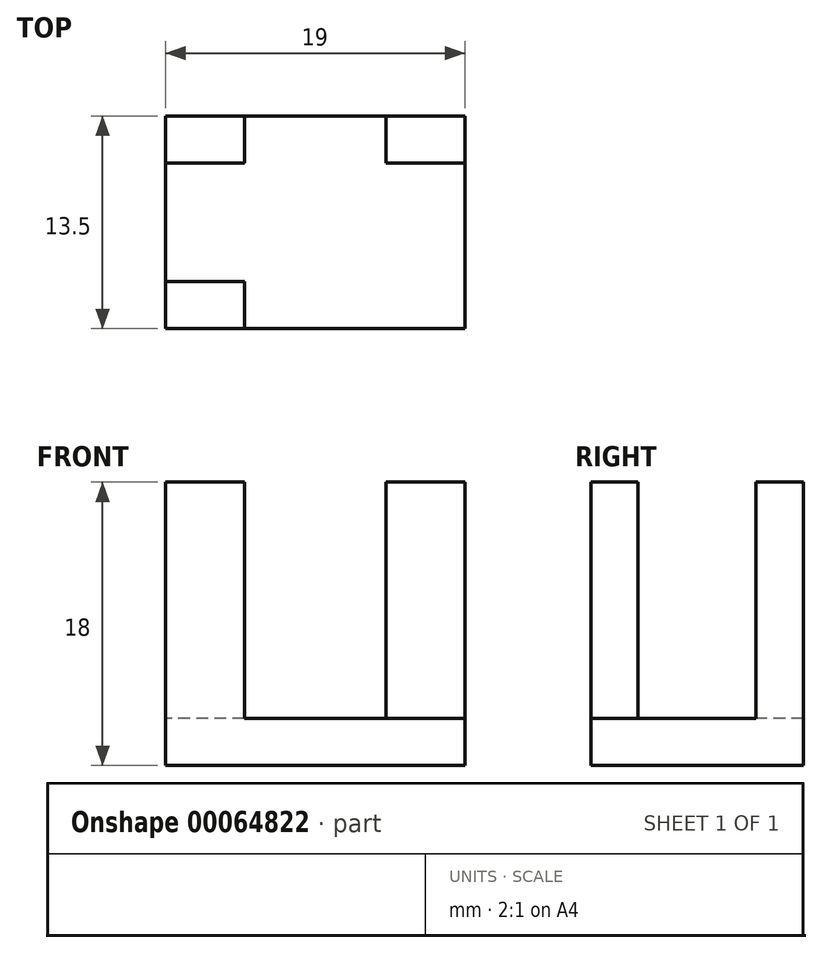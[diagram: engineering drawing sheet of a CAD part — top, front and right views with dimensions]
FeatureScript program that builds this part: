
annotation { "Feature Type Name" : "Feature", "Feature Type Description" : "" }
export const myFeature = defineFeature(function(context is Context, id is Id, definition is map)
    precondition{}
    {
        {
            var Q0;
            Q0=qCreatedBy(makeId("Top.planeOp"),FACE);
            var sketch = newSketch(context, id + "F0", { "sketchPlane" : qUnion([Q0])});
            skLineSegment(sketch, "E0.rect.bottom", {"start": v(-9.5, 6.75) * mm, "end": v(9.5, 6.75) * mm});
            skLineSegment(sketch, "E0.rect.top", {"start": v(-9.5, -6.75) * mm, "end": v(9.5, -6.75) * mm});
            skLineSegment(sketch, "E0.rect.left", {"start": v(-9.5, 6.75) * mm, "end": v(-9.5, -6.75) * mm});
            skLineSegment(sketch, "E0.rect.right", {"start": v(9.5, 6.75) * mm, "end": v(9.5, -6.75) * mm});
            skPoint(sketch, "E0.rect.middle", {"position": v(0, 0) * mm});
            skSolve(sketch);
        }
        {
            var Q0;
            Q0=makeQuery(id+"F0.imprint","IMPRINT",FACE,{"disambiguationData":[TD([[makeQuery(id+"F0.imprint","IMPRINT",EDGE,{"derivedFrom":sQuery(id+"F0.wireOp",EDGE,"E0.rect.bottom")}),-1.0]])]});
            extrude(context, id + "F1", {"entities" : qUnion([Q0]), "depth" : 3 * mm});
        }
        {
            var Q0;
            Q0=makeQuery(id+"F1.opExtrude","CAP_FACE",FACE,{"disambiguationData":[OSD([sQuery(id+"F0.wireOp",EDGE,"E0.rect.bottom"),sQuery(id+"F0.wireOp",EDGE,"E0.rect.top"),sQuery(id+"F0.wireOp",EDGE,"E0.rect.left"),sQuery(id+"F0.wireOp",EDGE,"E0.rect.right")])],"isStart":false});
            var sketch = newSketch(context, id + "F2", { "sketchPlane" : qUnion([Q0])});
            skLineSegment(sketch, "E1.bottom", {"start": v(9.5, 6.75) * mm, "end": v(4.5, 6.75) * mm});
            skLineSegment(sketch, "E1.top", {"start": v(9.5, -6.75) * mm, "end": v(4.5, -6.75) * mm});
            skLineSegment(sketch, "E1.left", {"start": v(9.5, 6.75) * mm, "end": v(9.5, -6.75) * mm});
            skLineSegment(sketch, "E1.right", {"start": v(4.5, 6.75) * mm, "end": v(4.5, -6.75) * mm});
            skLineSegment(sketch, "E2.top", {"start": v(9.5, 3.75) * mm, "end": v(4.5, 3.75) * mm});
            skLineSegment(sketch, "E2.left", {"start": v(9.5, 6.75) * mm, "end": v(9.5, 3.75) * mm});
            skLineSegment(sketch, "E2.right", {"start": v(4.5, 6.75) * mm, "end": v(4.5, 3.75) * mm});
            skLineSegment(sketch, "E3.bottom", {"start": v(4.5, -6.75) * mm, "end": v(9.5, -6.75) * mm});
            skLineSegment(sketch, "E3.top", {"start": v(4.5, -3.75) * mm, "end": v(9.5, -3.75) * mm});
            skLineSegment(sketch, "E3.left", {"start": v(4.5, -6.75) * mm, "end": v(4.5, -3.75) * mm});
            skLineSegment(sketch, "E3.right", {"start": v(9.5, -6.75) * mm, "end": v(9.5, -3.75) * mm});
            skLineSegment(sketch, "E4", {"start": v(0, -6.75) * mm, "end": v(0, 6.75) * mm});
            skLineSegment(sketch, "E5.MirrorCS", {"start": v(-9.5, 6.75) * mm, "end": v(-9.5, -6.75) * mm});
            skLineSegment(sketch, "E6.MirrorCS", {"start": v(-4.5, -3.75) * mm, "end": v(-9.5, -3.75) * mm});
            skLineSegment(sketch, "E7.MirrorCS", {"start": v(-9.5, 3.75) * mm, "end": v(-4.5, 3.75) * mm});
            skLineSegment(sketch, "E8.MirrorCS", {"start": v(-9.5, 6.75) * mm, "end": v(-4.5, 6.75) * mm});
            skLineSegment(sketch, "E9.MirrorCS", {"start": v(-4.5, 6.75) * mm, "end": v(-4.5, -6.75) * mm});
            skSolve(sketch);
        }
        {
            var Q0;
            Q0=makeQuery(id+"F2.imprint","IMPRINT",FACE,{"disambiguationData":[TD([[makeQuery(id+"F2.imprint","IMPRINT",EDGE,{"derivedFrom":sQuery(id+"F2.wireOp",EDGE,"E3.bottom")}),1.0]])]});
            var Q1;
            Q1=makeQuery(id+"F2.imprint","IMPRINT",FACE,{"disambiguationData":[TD([[makeQuery(id+"F2.imprint","IMPRINT",EDGE,{"derivedFrom":sQuery(id+"F2.wireOp",EDGE,"E1.bottom")}),-1.0]])]});
            var Q2;
            {var subQ3=sQuery(id+"F2.wireOp",EDGE,"E6.MirrorCS");Q2=makeQuery(id+"F2.imprint","IMPRINT",FACE,{"disambiguationData":[TD([[makeQuery(id+"F2.imprint","IMPRINT",EDGE,{"derivedFrom":subQ3}),1.0]])]});}
            var Q3;
            {var subQ2=sQuery(id+"F2.wireOp",EDGE,"E7.MirrorCS");Q3=makeQuery(id+"F2.imprint","IMPRINT",FACE,{"disambiguationData":[TD([[makeQuery(id+"F2.imprint","IMPRINT",EDGE,{"derivedFrom":subQ2}),1.0]])]});}
            extrude(context, id + "F3", {"entities" : qUnion([Q0, Q1, Q2, Q3]), "operationType" : NewBodyOperationType.ADD, "depth" : 15 * mm});
        }
    });
